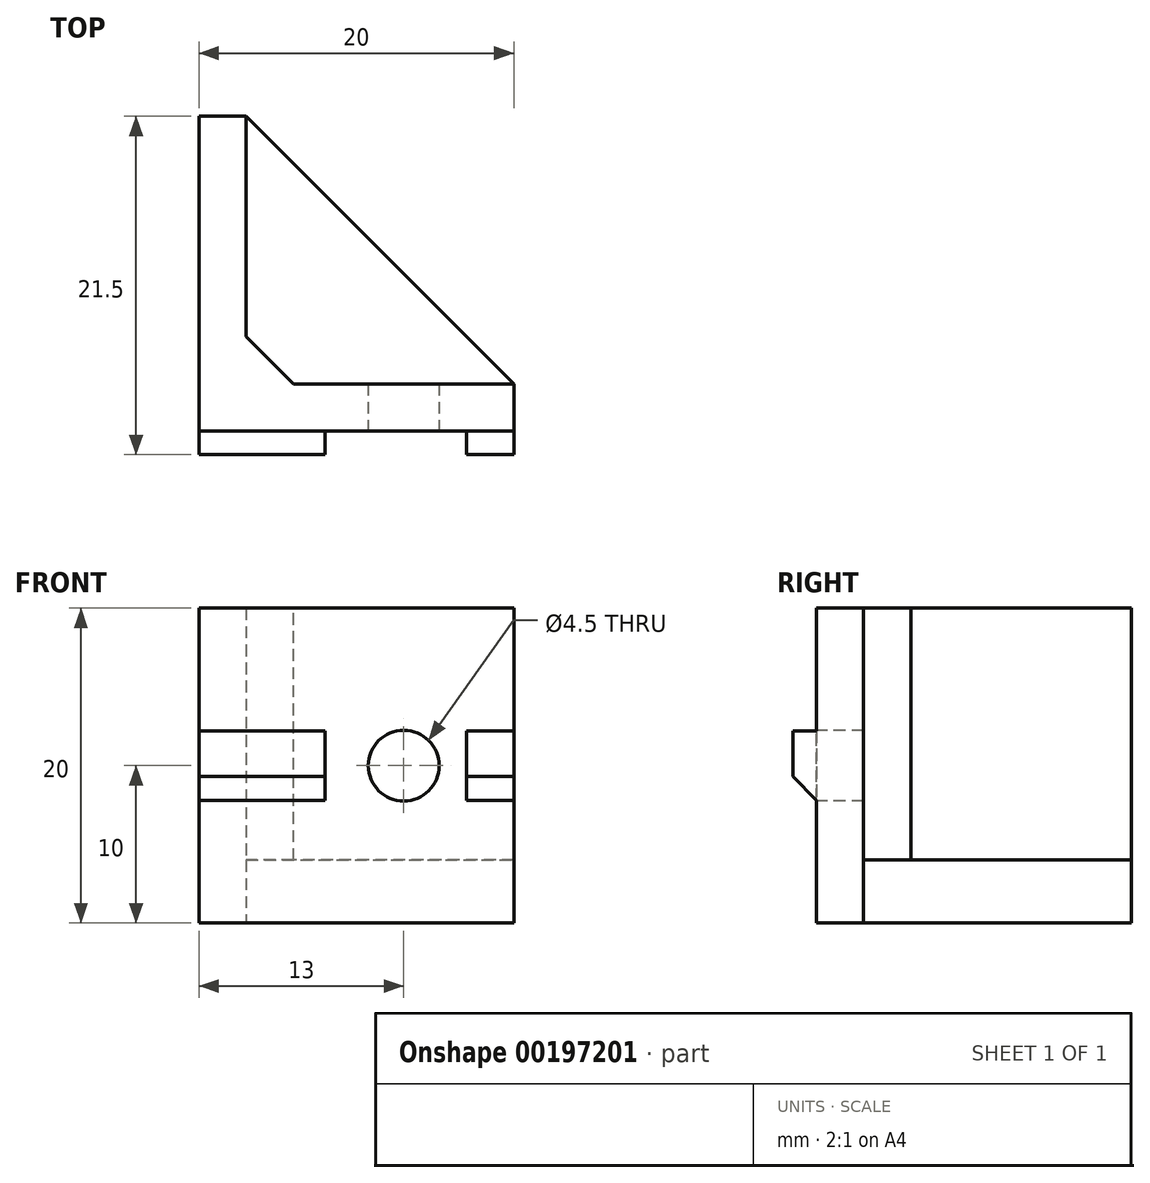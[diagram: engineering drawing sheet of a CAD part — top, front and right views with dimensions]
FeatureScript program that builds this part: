
annotation { "Feature Type Name" : "Feature", "Feature Type Description" : "" }
export const myFeature = defineFeature(function(context is Context, id is Id, definition is map)
    precondition{}
    {
        {
            var Q0;
            Q0=qCreatedBy(makeId("Top.planeOp"),FACE);
            var sketch = newSketch(context, id + "F0", { "sketchPlane" : qUnion([Q0])});
            skLineSegment(sketch, "E0", {"start": v(0, 0) * mm, "end": v(20, 0) * mm});
            skLineSegment(sketch, "E1", {"start": v(0, 20) * mm, "end": v(0, 0) * mm});
            skLineSegment(sketch, "E2", {"start": v(0, 20) * mm, "end": v(3, 20) * mm});
            skLineSegment(sketch, "E3", {"start": v(3, 20) * mm, "end": v(20, 3) * mm});
            skLineSegment(sketch, "E4", {"start": v(20, 3) * mm, "end": v(20, 0) * mm});
            skLineSegment(sketch, "E5", {"start": v(20, 3) * mm, "end": v(3, 3) * mm});
            skLineSegment(sketch, "E6", {"start": v(3, 3) * mm, "end": v(3, 20) * mm});
            skSolve(sketch);
        }
        {
            var Q0;
            Q0=makeQuery(id+"F0.imprint","IMPRINT",FACE,{"disambiguationData":[TD([[makeQuery(id+"F0.imprint","IMPRINT",EDGE,{"derivedFrom":sQuery(id+"F0.wireOp",EDGE,"E0")}),1.0]])]});
            extrude(context, id + "F1", {"entities" : qUnion([Q0]), "depth" : 20 * mm});
        }
        {
            var Q0;
            Q0=makeQuery(id+"F0.imprint","IMPRINT",FACE,{"disambiguationData":[TD([[makeQuery(id+"F0.imprint","IMPRINT",EDGE,{"derivedFrom":sQuery(id+"F0.wireOp",EDGE,"E3")}),-1.0]])]});
            extrude(context, id + "F2", {"entities" : qUnion([Q0]), "operationType" : NewBodyOperationType.ADD, "depth" : 4 * mm});
        }
        {
            var Q0;
            Q0=makeQuery(id+"F1.opExtrude","SWEPT_FACE",FACE,{"disambiguationData":[OSD([sQuery(id+"F0.wireOp",EDGE,"E0")])]});
            var sketch = newSketch(context, id + "F3", { "sketchPlane" : qUnion([Q0])});
            skCircle(sketch, "E7", {"center": v(13, 10) * mm, "radius": 2.25 * mm});
            skLineSegment(sketch, "E8.bottom", {"start": v(0, 12.2) * mm, "end": v(8, 12.2) * mm});
            skLineSegment(sketch, "E8.top", {"start": v(0, 7.8) * mm, "end": v(8, 7.8) * mm});
            skLineSegment(sketch, "E8.left", {"start": v(0, 12.2) * mm, "end": v(0, 7.8) * mm});
            skLineSegment(sketch, "E8.right", {"start": v(8, 12.2) * mm, "end": v(8, 7.8) * mm});
            skPoint(sketch, "E8.middle", {"position": v(4, 10) * mm});
            skPoint(sketch, "E8.middle.positionSnap0", {"position": v(0, 10) * mm});
            skPoint(sketch, "E8.centerSnap0", {"position": v(0, 10) * mm});
            skLineSegment(sketch, "E9.bottom", {"start": v(20, 12.2) * mm, "end": v(17, 12.2) * mm});
            skLineSegment(sketch, "E9.top", {"start": v(20, 7.8) * mm, "end": v(17, 7.8) * mm});
            skLineSegment(sketch, "E9.left", {"start": v(20, 12.2) * mm, "end": v(20, 7.8) * mm});
            skLineSegment(sketch, "E9.right", {"start": v(17, 12.2) * mm, "end": v(17, 7.8) * mm});
            skPoint(sketch, "E9.middle", {"position": v(18.5, 10) * mm});
            skPoint(sketch, "E9.middle.positionSnap0", {"position": v(20, 10) * mm});
            skPoint(sketch, "E9.cornerSnap0", {"position": v(20, 10) * mm});
            skPoint(sketch, "E9.centerSnap0", {"position": v(20, 10) * mm});
            skSolve(sketch);
        }
        {
            var Q0;
            Q0=makeQuery(id+"F3.imprint","IMPRINT",FACE,{"disambiguationData":[TD([[makeQuery(id+"F3.imprint","IMPRINT",EDGE,{"derivedFrom":sQuery(id+"F3.wireOp",EDGE,"E7")}),1.0]])]});
            extrude(context, id + "F4", {"entities" : qUnion([Q0]), "operationType" : NewBodyOperationType.REMOVE, "endBound" : BoundingType.UP_TO_NEXT, "oppositeDirection" : true, "depth" : 25 * mm});
        }
        {
            var Q0;
            Q0=makeQuery(id+"F3.imprint","IMPRINT",FACE,{"disambiguationData":[TD([[makeQuery(id+"F3.imprint","IMPRINT",EDGE,{"derivedFrom":sQuery(id+"F3.wireOp",EDGE,"E8.bottom")}),-1.0]])]});
            var Q1;
            Q1=makeQuery(id+"F3.imprint","IMPRINT",FACE,{"disambiguationData":[TD([[makeQuery(id+"F3.imprint","IMPRINT",EDGE,{"derivedFrom":sQuery(id+"F3.wireOp",EDGE,"E9.bottom")}),1.0]])]});
            extrude(context, id + "F5", {"entities" : qUnion([Q0, Q1]), "operationType" : NewBodyOperationType.ADD, "depth" : 1.5 * mm});
        }
        {
            var Q0;
            Q0=makeQuery(id+"F5.opExtrude","CAP_EDGE",EDGE,{"disambiguationData":[OSD([sQuery(id+"F3.wireOp",EDGE,"E8.top")])],"isStart":false});
            var Q1;
            Q1=makeQuery(id+"F5.opExtrude","CAP_EDGE",EDGE,{"disambiguationData":[OSD([sQuery(id+"F3.wireOp",EDGE,"E9.top")])],"isStart":false});
            chamfer(context, id + "F6", {"entities" : qUnion([Q0, Q1]), "width" : 1.5 * mm, "tangentPropagation" : true});
        }
        {
            var Q0;
            Q0=qCreatedBy(makeId("Front.planeOp"),FACE);
            var Q1;
            Q1=qCreatedBy(makeId("Right.planeOp"),FACE);
            cPlane(context, id + "F7", {"entities" : qUnion([Q0, Q1]), "cplaneType" : CPlaneType.MID_PLANE, "offset" : 25 * mm, "flipAlignment" : true, "width" : 150 * mm, "height" : 150 * mm});
        }
        {
            var Q0;
            Q0=makeQuery(id+"F1.opExtrude","SWEPT_EDGE",EDGE,{"disambiguationData":[OSD([sQuery(id+"F0.wireOp",EDGE,"E5"),sQuery(id+"F0.wireOp",EDGE,"E6")])]});
            chamfer(context, id + "F8", {"entities" : qUnion([Q0]), "width" : 3 * mm, "tangentPropagation" : true});
        }
    });
